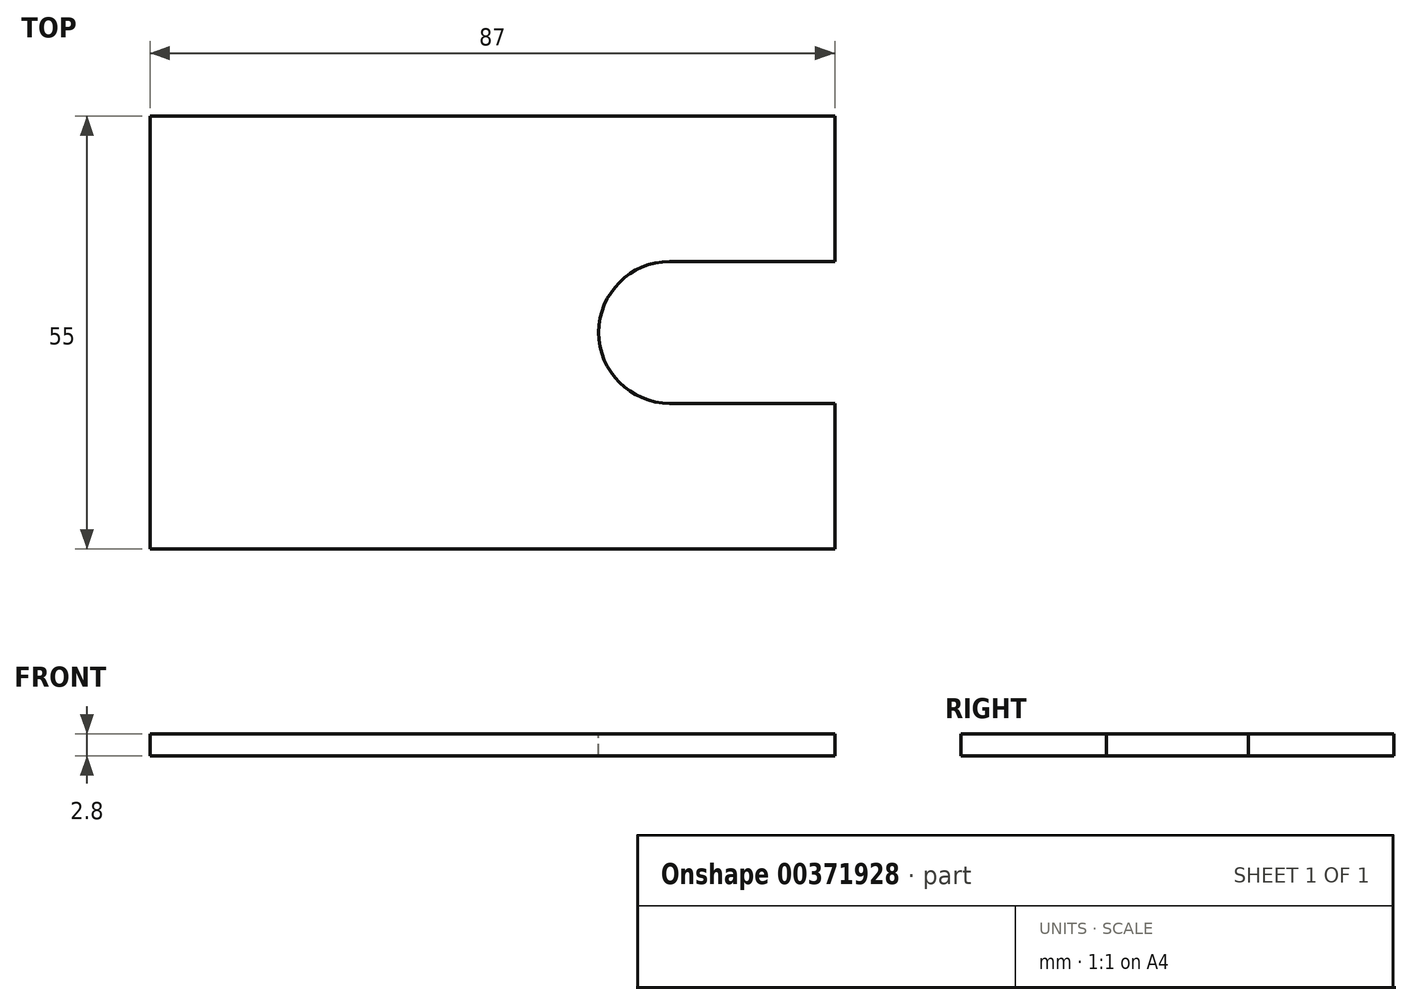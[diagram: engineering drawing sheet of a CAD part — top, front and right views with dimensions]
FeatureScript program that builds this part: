
annotation { "Feature Type Name" : "Feature", "Feature Type Description" : "" }
export const myFeature = defineFeature(function(context is Context, id is Id, definition is map)
    precondition{}
    {
        {
            var Q0;
            Q0=qCreatedBy(makeId("Top.planeOp"),FACE);
            var sketch = newSketch(context, id + "F0", { "sketchPlane" : qUnion([Q0])});
            skLineSegment(sketch, "E0.bottom", {"start": v(-43.5, 27.5) * mm, "end": v(43.5, 27.5) * mm});
            skLineSegment(sketch, "E0.top", {"start": v(-43.5, -27.5) * mm, "end": v(43.5, -27.5) * mm});
            skLineSegment(sketch, "E0.left", {"start": v(-43.5, 27.5) * mm, "end": v(-43.5, -27.5) * mm});
            skLineSegment(sketch, "E0.right", {"start": v(43.5, 27.5) * mm, "end": v(43.5, -27.5) * mm});
            skPoint(sketch, "E0.middle", {"position": v(0, 0) * mm});
            skSolve(sketch);
        }
        {
            var Q0;
            Q0 = qSketchRegion(id + "F0", true);
            extrude(context, id + "F1", {"entities" : qUnion([Q0]), "depth" : 2.8 * mm, "offsetDistance" : 25 * mm});
        }
        {
            var Q0;
            Q0=makeQuery(id+"F1.opExtrude","CAP_FACE",FACE,{"disambiguationData":[OSD([sQuery(id+"F0.wireOp",EDGE,"E0.bottom"),sQuery(id+"F0.wireOp",EDGE,"E0.top"),sQuery(id+"F0.wireOp",EDGE,"E0.left"),sQuery(id+"F0.wireOp",EDGE,"E0.right")])],"isStart":false});
            var sketch = newSketch(context, id + "F2", { "sketchPlane" : qUnion([Q0])});
            skLineSegment(sketch, "E1.bottom", {"start": v(13.5, 9) * mm, "end": v(73.5, 9) * mm});
            skLineSegment(sketch, "E1.top", {"start": v(13.5, -9) * mm, "end": v(73.5, -9) * mm});
            skLineSegment(sketch, "E1.left", {"start": v(13.5, 9) * mm, "end": v(13.5, -9) * mm});
            skLineSegment(sketch, "E1.right", {"start": v(73.5, 9) * mm, "end": v(73.5, -9) * mm});
            skPoint(sketch, "E1.middle", {"position": v(43.5, 0) * mm});
            skSolve(sketch);
        }
        {
            var Q0;
            Q0 = qSketchRegion(id + "F2", true);
            extrude(context, id + "F3", {"entities" : qUnion([Q0]), "operationType" : NewBodyOperationType.REMOVE, "oppositeDirection" : true, "depth" : 25 * mm, "offsetDistance" : 25 * mm});
        }
        {
            var Q0;
            Q0=makeQuery(id+"F3.boolean.opBoolean","COPY",EDGE,{"derivedFrom":makeQuery(id+"F3.opExtrude","SWEPT_EDGE",EDGE,{"disambiguationData":[OSD([sQuery(id+"F2.wireOp",EDGE,"E1.bottom"),sQuery(id+"F2.wireOp",EDGE,"E1.left")])]})});
            var Q1;
            Q1=makeQuery(id+"F3.boolean.opBoolean","COPY",EDGE,{"derivedFrom":makeQuery(id+"F3.opExtrude","SWEPT_EDGE",EDGE,{"disambiguationData":[OSD([sQuery(id+"F2.wireOp",EDGE,"E1.top"),sQuery(id+"F2.wireOp",EDGE,"E1.left")])]})});
            fillet(context, id + "F4", {"entities" : qUnion([Q0, Q1]), "radius" : 9 * mm, "tangentPropagation" : true, "allowEdgeOverflow" : false});
        }
    });
